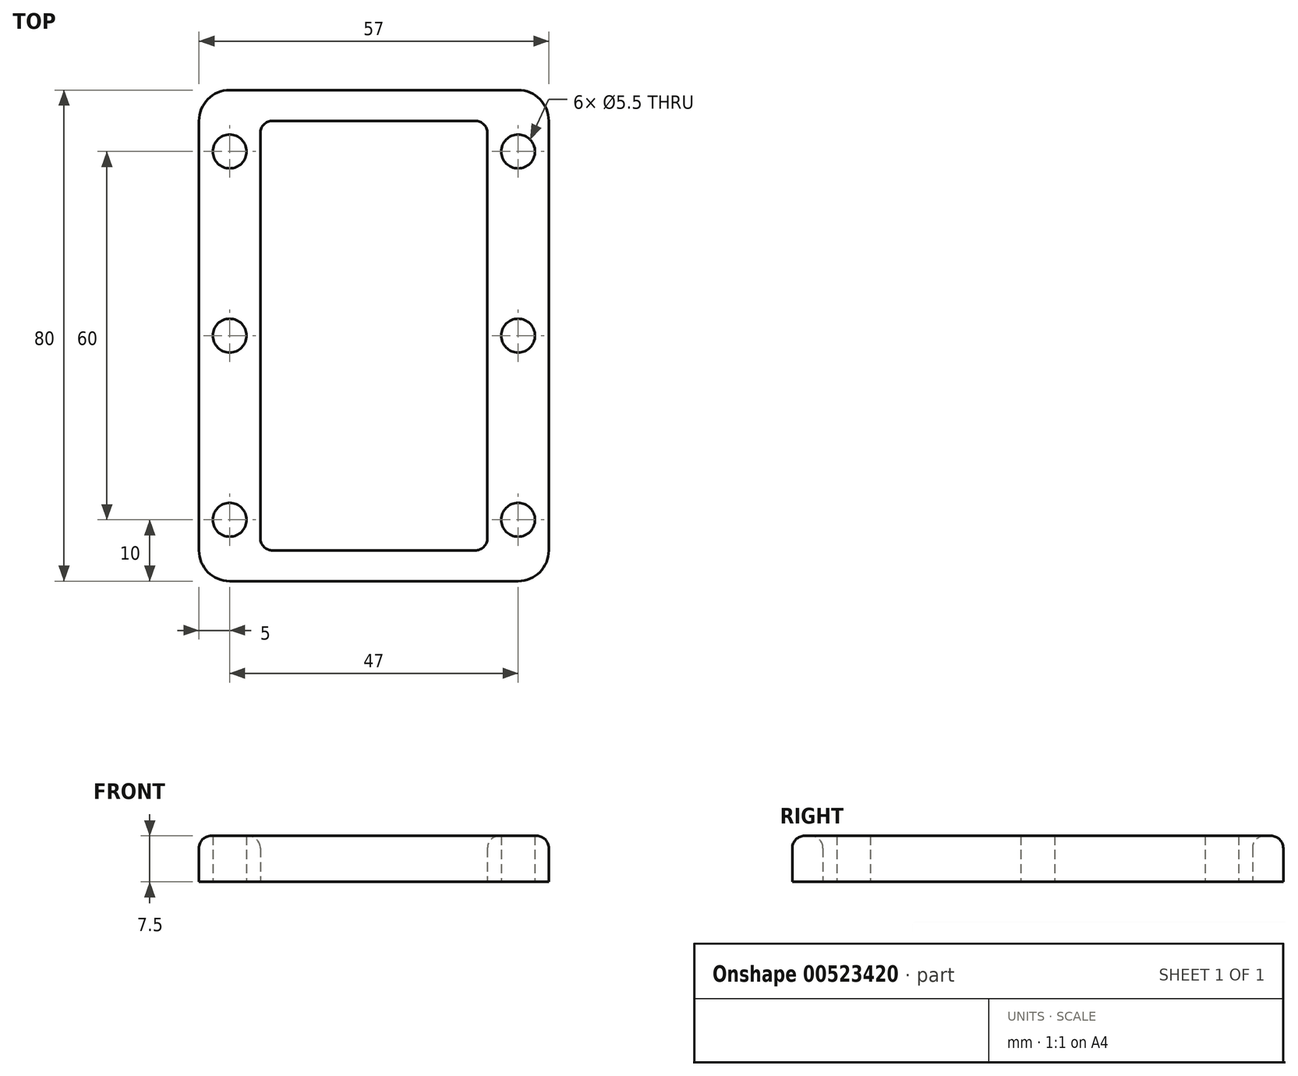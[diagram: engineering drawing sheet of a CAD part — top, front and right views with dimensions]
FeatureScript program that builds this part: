
annotation { "Feature Type Name" : "Feature", "Feature Type Description" : "" }
export const myFeature = defineFeature(function(context is Context, id is Id, definition is map)
    precondition{}
    {
        {
            var Q0;
            Q0=qCreatedBy(makeId("Top.planeOp"),FACE);
            var sketch = newSketch(context, id + "F0", { "sketchPlane" : qUnion([Q0])});
            skLineSegment(sketch, "E0.bottom", {"start": v(-23.5, 40) * mm, "end": v(23.5, 40) * mm});
            skLineSegment(sketch, "E0.top", {"start": v(-23.5, -40) * mm, "end": v(23.5, -40) * mm});
            skLineSegment(sketch, "E0.left", {"start": v(-28.5, 35) * mm, "end": v(-28.5, -35) * mm});
            skLineSegment(sketch, "E0.right", {"start": v(28.5, 35) * mm, "end": v(28.5, -35) * mm});
            skLineSegment(sketch, "E1", {"start": v(0, 40) * mm, "end": v(0, -40) * mm, "construction": true});
            skPoint(sketch, "E2.visualSharp", {"position": v(-28.5, 40) * mm});
            skArc(sketch, "E2.filletArc", {"start": v(-23.5, 40) * mm, "mid": v(-27.04, 38.54) * mm, "end": v(-28.5, 35) * mm});
            skPoint(sketch, "E3.visualSharp", {"position": v(28.5, 40) * mm});
            skArc(sketch, "E3.filletArc", {"start": v(28.5, 35) * mm, "mid": v(27.04, 38.54) * mm, "end": v(23.5, 40) * mm});
            skPoint(sketch, "E4.visualSharp", {"position": v(-28.5, -40) * mm});
            skArc(sketch, "E4.filletArc", {"start": v(-28.5, -35) * mm, "mid": v(-27.04, -38.54) * mm, "end": v(-23.5, -40) * mm});
            skPoint(sketch, "E5.visualSharp", {"position": v(28.5, -40) * mm});
            skArc(sketch, "E5.filletArc", {"start": v(23.5, -40) * mm, "mid": v(27.04, -38.54) * mm, "end": v(28.5, -35) * mm});
            skLineSegment(sketch, "E6.bottom", {"start": v(-16.5, 35) * mm, "end": v(16.5, 35) * mm});
            skLineSegment(sketch, "E6.top", {"start": v(-16.5, -35) * mm, "end": v(16.5, -35) * mm});
            skLineSegment(sketch, "E6.left", {"start": v(-18.5, 33) * mm, "end": v(-18.5, -33) * mm});
            skLineSegment(sketch, "E6.right", {"start": v(18.5, 33) * mm, "end": v(18.5, -33) * mm});
            skLineSegment(sketch, "E7", {"start": v(0, 35) * mm, "end": v(0, -35) * mm, "construction": true});
            skLineSegment(sketch, "E8", {"start": v(0, 35) * mm, "end": v(0, 40) * mm, "construction": true});
            skLineSegment(sketch, "E9", {"start": v(-28.5, 0) * mm, "end": v(-18.5, 0) * mm, "construction": true});
            skPoint(sketch, "E10.visualSharp", {"position": v(-18.5, 35) * mm});
            skArc(sketch, "E10.filletArc", {"start": v(-16.5, 35) * mm, "mid": v(-17.91, 34.41) * mm, "end": v(-18.5, 33) * mm});
            skPoint(sketch, "E11.visualSharp", {"position": v(18.5, 35) * mm});
            skArc(sketch, "E11.filletArc", {"start": v(18.5, 33) * mm, "mid": v(17.91, 34.41) * mm, "end": v(16.5, 35) * mm});
            skPoint(sketch, "E12.visualSharp", {"position": v(18.5, -35) * mm});
            skArc(sketch, "E12.filletArc", {"start": v(16.5, -35) * mm, "mid": v(17.91, -34.41) * mm, "end": v(18.5, -33) * mm});
            skPoint(sketch, "E13.visualSharp", {"position": v(-18.5, -35) * mm});
            skArc(sketch, "E13.filletArc", {"start": v(-18.5, -33) * mm, "mid": v(-17.91, -34.41) * mm, "end": v(-16.5, -35) * mm});
            skCircle(sketch, "E14", {"center": v(-23.5, 30) * mm, "radius": 2.75 * mm});
            skCircle(sketch, "E15", {"center": v(-23.5, -30) * mm, "radius": 2.75 * mm});
            skCircle(sketch, "E16", {"center": v(-23.5, 0) * mm, "radius": 2.75 * mm});
            skLineSegment(sketch, "E17", {"start": v(-23.5, 30) * mm, "end": v(-23.5, -30) * mm, "construction": true});
            skCircle(sketch, "E18.MirrorC", {"center": v(23.5, 30) * mm, "radius": 2.75 * mm});
            skCircle(sketch, "E19.MirrorC", {"center": v(23.5, 0) * mm, "radius": 2.75 * mm});
            skCircle(sketch, "E20.MirrorC", {"center": v(23.5, -30) * mm, "radius": 2.75 * mm});
            skSolve(sketch);
        }
        {
            var Q0;
            Q0=qSketchRegion(id+"F0",true);
            extrude(context, id + "F1", {"entities" : qUnion([Q0]), "depth" : 7.5 * mm, "offsetDistance" : 25 * mm});
        }
        {
            var Q0;
            Q0=makeQuery(id+"F1.opExtrude","CAP_EDGE",EDGE,{"disambiguationData":[OSD([sQuery(id+"F0.wireOp",EDGE,"E6.left")])],"isStart":false});
            var Q1;
            Q1=makeQuery(id+"F1.opExtrude","CAP_EDGE",EDGE,{"disambiguationData":[OSD([sQuery(id+"F0.wireOp",EDGE,"E0.top")])],"isStart":false});
            fillet(context, id + "F2", {"entities" : qUnion([Q0, Q1]), "tangentPropagation" : true, "radius" : 2 * mm, "defaultsChanged" : true, "vertexSettings" : [], "allowEdgeOverflow" : false});
        }
    });
